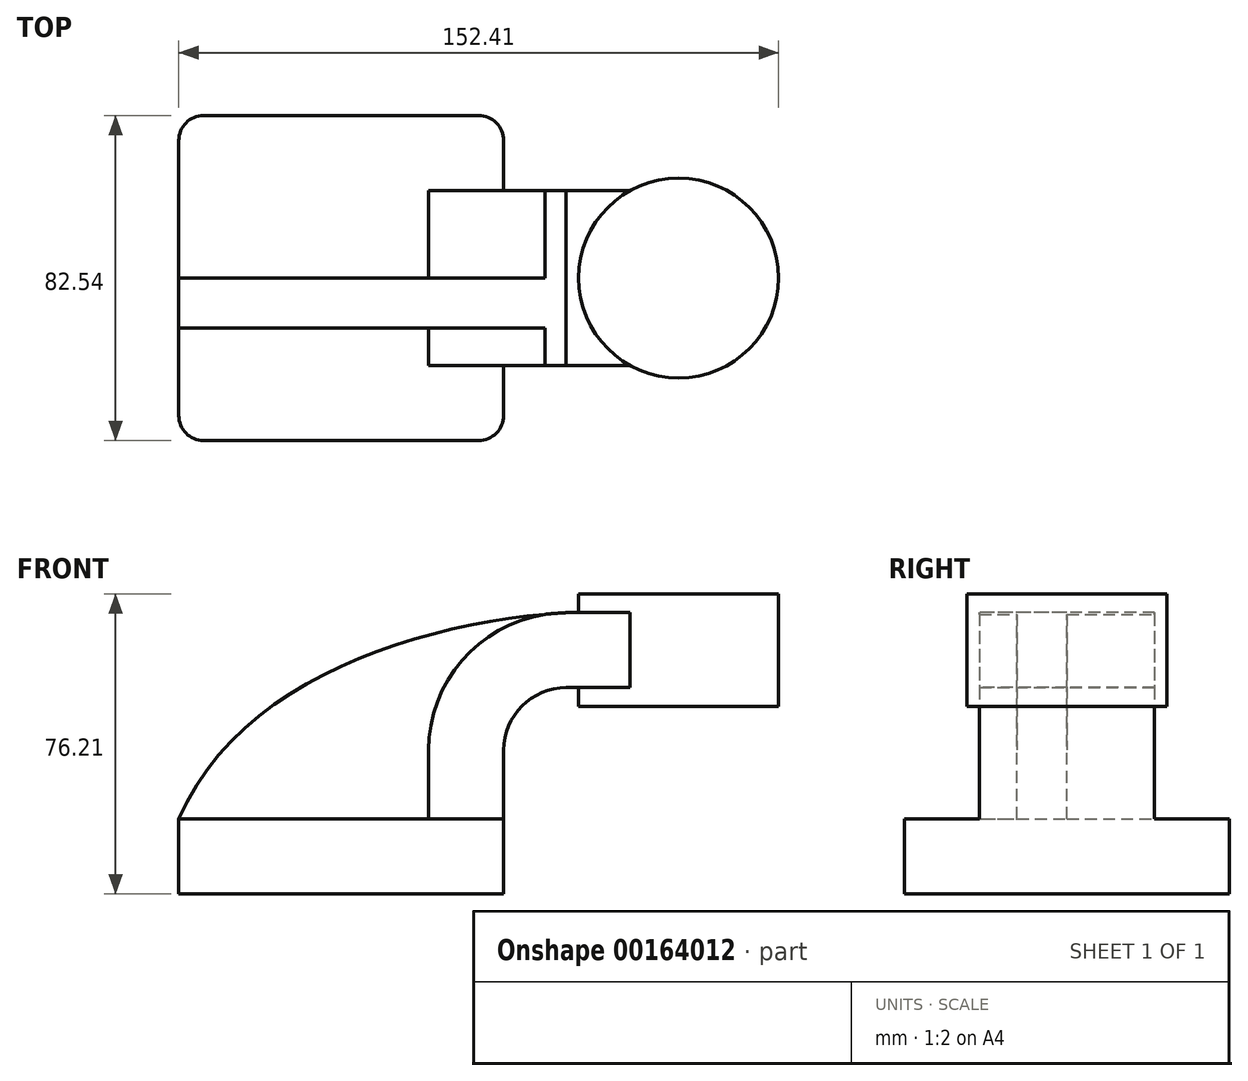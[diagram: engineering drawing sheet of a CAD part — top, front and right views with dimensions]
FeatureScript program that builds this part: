
annotation { "Feature Type Name" : "Feature", "Feature Type Description" : "" }
export const myFeature = defineFeature(function(context is Context, id is Id, definition is map)
    precondition{}
    {
        {
            var Q0;
            Q0=qCreatedBy(makeId("Front.planeOp"),FACE);
            var sketch = newSketch(context, id + "F0", { "sketchPlane" : qUnion([Q0])});
            skLineSegment(sketch, "E0.bottom", {"start": v(-41.28, -9.53) * mm, "end": v(41.28, -9.53) * mm});
            skLineSegment(sketch, "E0.top", {"start": v(-41.28, 9.52) * mm, "end": v(41.28, 9.52) * mm});
            skLineSegment(sketch, "E0.left", {"start": v(-41.27, -9.53) * mm, "end": v(-41.28, 9.52) * mm});
            skLineSegment(sketch, "E0.right", {"start": v(41.28, -9.53) * mm, "end": v(41.28, 9.52) * mm});
            skPoint(sketch, "E0.middle", {"position": v(0, 0) * mm});
            skLineSegment(sketch, "E1.bottom", {"start": v(60.32, 38.1) * mm, "end": v(111.12, 38.1) * mm});
            skLineSegment(sketch, "E1.top", {"start": v(60.32, 66.67) * mm, "end": v(111.12, 66.67) * mm});
            skLineSegment(sketch, "E1.left", {"start": v(60.32, 38.1) * mm, "end": v(60.32, 66.67) * mm});
            skLineSegment(sketch, "E1.right", {"start": v(111.12, 38.1) * mm, "end": v(111.12, 66.67) * mm});
            skPoint(sketch, "E1.middle", {"position": v(85.72, 52.39) * mm});
            skLineSegment(sketch, "E2", {"start": v(41.27, 9.52) * mm, "end": v(41.27, 27) * mm});
            skArc(sketch, "E3", {"start": v(41.27, 27) * mm, "mid": v(45.92, 38.23) * mm, "end": v(57.15, 42.88) * mm});
            skLineSegment(sketch, "E4", {"start": v(57.15, 42.88) * mm, "end": v(85.73, 42.88) * mm});
            skLineSegment(sketch, "E5", {"start": v(85.73, 42.88) * mm, "end": v(85.73, 66.67) * mm});
            skLineSegment(sketch, "E6.0", {"start": v(57.15, 61.93) * mm, "end": v(85.73, 61.93) * mm});
            skArc(sketch, "E6.1", {"start": v(22.23, 27) * mm, "mid": v(32.45, 51.7) * mm, "end": v(57.15, 61.93) * mm});
            skLineSegment(sketch, "E6.2", {"start": v(22.23, 9.52) * mm, "end": v(22.23, 27) * mm});
            skLineSegment(sketch, "E7", {"start": v(85.72, 66.67) * mm, "end": v(85.72, 38.1) * mm});
            skFitSpline(sketch, "E8", {"points": [v(-41.28, 9.53) * mm, v(57.15, 61.93) * mm], "startDerivative": vector(46.77, 108.75) * mm, "endDerivative": vector(107.47, 6.6) * mm});
            skSolve(sketch);
        }
        {
            var Q0;
            Q0=makeQuery(id+"F0.imprint","IMPRINT",FACE,{"disambiguationData":[TD([[makeQuery(id+"F0.imprint","IMPRINT",EDGE,{"derivedFrom":sQuery(id+"F0.wireOp",EDGE,"E0.bottom")}),1.0]])]});
            extrude(context, id + "F1", {"entities" : qUnion([Q0]), "endBound" : BoundingType.SYMMETRIC, "depth" : 82.55 * mm});
        }
        {
            var Q0;
            {var subQ1=sQuery(id+"F0.wireOp",EDGE,"E2");Q0=makeQuery(id+"F0.imprint","IMPRINT",FACE,{"disambiguationData":[TD([[makeQuery(id+"F0.imprint","IMPRINT",EDGE,{"derivedFrom":subQ1}),1.0]])]});}
            var Q1;
            {var subQ0=sQuery(id+"F0.wireOp",EDGE,"E4");var subQ1=sQuery(id+"F0.wireOp",EDGE,"E1.left");var subQ2=makeQuery(id+"F0.imprint","INTERSECT",VERTEX,{"derivedFrom":[subQ1,subQ0]});Q1=makeQuery(id+"F0.imprint","IMPRINT",FACE,{"disambiguationData":[TD([[makeQuery(id+"F0.imprint","IMPRINT",EDGE,{"disambiguationData":[TD([[subQ2,-1.0]])],"derivedFrom":subQ1}),-1.0]])]});}
            extrude(context, id + "F2", {"entities" : qUnion([Q0, Q1]), "operationType" : NewBodyOperationType.ADD, "endBound" : BoundingType.SYMMETRIC, "depth" : 44.45 * mm});
        }
        {
            var Q0;
            {var subQ0=sQuery(id+"F0.wireOp",EDGE,"E1.right");Q0=makeQuery(id+"F0.imprint","IMPRINT",FACE,{"disambiguationData":[TD([[makeQuery(id+"F0.imprint","IMPRINT",EDGE,{"derivedFrom":subQ0}),1.0]])]});}
            var Q1;
            Q1=sQuery(id+"F0.wireOp",EDGE,"E5");
            revolve(context, id + "F3", {"operationType" : NewBodyOperationType.ADD, "entities" : qUnion([Q0]), "axis" : qUnion([Q1]), "revolveType" : RevolveType.FULL});
        }
        {
            var Q0;
            {var subQ3=sQuery(id+"F0.wireOp",EDGE,"E6.2");Q0=makeQuery(id+"F0.imprint","IMPRINT",FACE,{"disambiguationData":[TD([[makeQuery(id+"F0.imprint","IMPRINT",EDGE,{"derivedFrom":subQ3}),1.0]])]});}
            extrude(context, id + "F4", {"entities" : qUnion([Q0]), "operationType" : NewBodyOperationType.ADD, "depth" : 12.7 * mm});
        }
        {
            var Q0;
            Q0=makeQuery(id+"F1.opExtrude","CAP_EDGE",EDGE,{"disambiguationData":[OSD([sQuery(id+"F0.wireOp",EDGE,"E0.right")])],"isStart":false});
            var Q1;
            Q1=makeQuery(id+"F1.opExtrude","CAP_EDGE",EDGE,{"disambiguationData":[OSD([sQuery(id+"F0.wireOp",EDGE,"E0.left")])],"isStart":false});
            var Q2;
            Q2=makeQuery(id+"F1.opExtrude","CAP_EDGE",EDGE,{"disambiguationData":[OSD([sQuery(id+"F0.wireOp",EDGE,"E0.right")])],"isStart":true});
            var Q3;
            Q3=makeQuery(id+"F1.opExtrude","CAP_EDGE",EDGE,{"disambiguationData":[OSD([sQuery(id+"F0.wireOp",EDGE,"E0.left")])],"isStart":true});
            fillet(context, id + "F5", {"entities" : qUnion([Q0, Q1, Q2, Q3]), "radius" : 6.35 * mm, "tangentPropagation" : true, "allowEdgeOverflow" : false});
        }
    });
